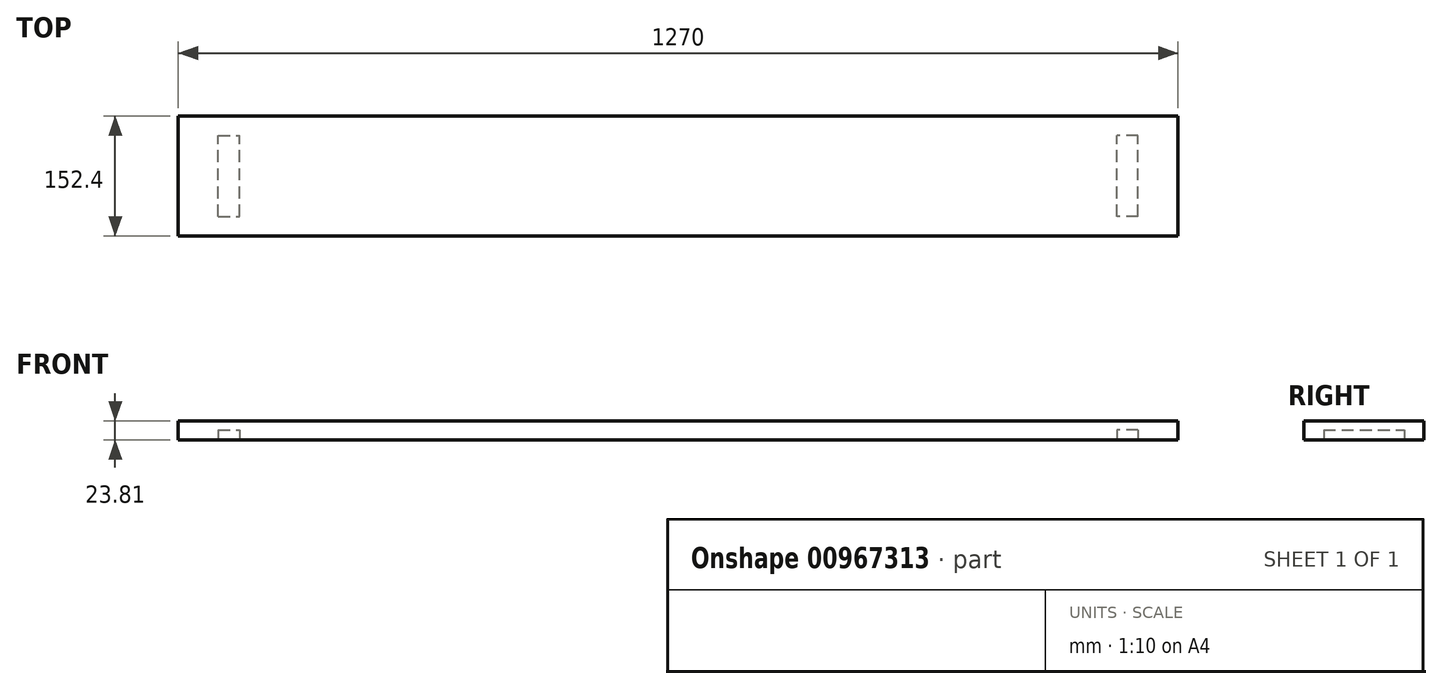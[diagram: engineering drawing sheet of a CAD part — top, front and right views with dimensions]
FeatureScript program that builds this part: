
annotation { "Feature Type Name" : "Feature", "Feature Type Description" : "" }
export const myFeature = defineFeature(function(context is Context, id is Id, definition is map)
    precondition{}
    {
        {
            var Q0;
            Q0=qCreatedBy(makeId("Top.planeOp"),FACE);
            var sketch = newSketch(context, id + "F0", { "sketchPlane" : qUnion([Q0])});
            skLineSegment(sketch, "E0.bottom", {"start": v(-909.25, -64.28) * mm, "end": v(360.75, -64.28) * mm});
            skLineSegment(sketch, "E0.top", {"start": v(-909.25, -216.68) * mm, "end": v(360.75, -216.68) * mm});
            skLineSegment(sketch, "E0.left", {"start": v(-909.25, -64.28) * mm, "end": v(-909.25, -216.68) * mm});
            skLineSegment(sketch, "E0.right", {"start": v(360.75, -64.28) * mm, "end": v(360.75, -216.68) * mm});
            skSolve(sketch);
        }
        {
            var Q0;
            Q0=makeQuery(id+"F0.imprint","IMPRINT",FACE,{"disambiguationData":[TD([[makeQuery(id+"F0.imprint","IMPRINT",EDGE,{"derivedFrom":sQuery(id+"F0.wireOp",EDGE,"E0.bottom")}),-1.0]])]});
            extrude(context, id + "F1", {"entities" : qUnion([Q0]), "depth" : 23.8 * mm, "offsetDistance" : 25.4 * mm});
        }
        {
            var Q0;
            Q0=makeQuery(id+"F1.opExtrude","CAP_FACE",FACE,{"disambiguationData":[OSD([sQuery(id+"F0.wireOp",EDGE,"E0.bottom"),sQuery(id+"F0.wireOp",EDGE,"E0.top"),sQuery(id+"F0.wireOp",EDGE,"E0.left"),sQuery(id+"F0.wireOp",EDGE,"E0.right")])],"isStart":true});
            var sketch = newSketch(context, id + "F2", { "sketchPlane" : qUnion([Q0])});
            skLineSegment(sketch, "E1.bottom", {"start": v(-858.45, 191.68) * mm, "end": v(-831.46, 191.68) * mm});
            skLineSegment(sketch, "E1.top", {"start": v(-858.45, 89.28) * mm, "end": v(-831.46, 89.28) * mm});
            skLineSegment(sketch, "E1.left", {"start": v(-858.45, 191.68) * mm, "end": v(-858.45, 89.28) * mm});
            skLineSegment(sketch, "E1.right", {"start": v(-831.46, 191.68) * mm, "end": v(-831.46, 89.28) * mm});
            skPoint(sketch, "E2", {"position": v(-909.25, 140.48) * mm});
            skPoint(sketch, "E3", {"position": v(-858.45, 140.48) * mm});
            skLineSegment(sketch, "E4", {"start": v(-274.25, 64.28) * mm, "end": v(-274.25, 216.68) * mm, "construction": true});
            skLineSegment(sketch, "E5.MirrorCS", {"start": v(282.97, 191.68) * mm, "end": v(282.97, 89.28) * mm});
            skLineSegment(sketch, "E6.MirrorCS", {"start": v(309.95, 89.28) * mm, "end": v(282.97, 89.28) * mm});
            skLineSegment(sketch, "E7.MirrorCS", {"start": v(309.95, 191.68) * mm, "end": v(309.95, 89.28) * mm});
            skLineSegment(sketch, "E8.MirrorCS", {"start": v(309.95, 191.68) * mm, "end": v(282.97, 191.68) * mm});
            skSolve(sketch);
        }
        {
            var Q0;
            Q0 = qSketchRegion(id + "F2", true);
            extrude(context, id + "F3", {"entities" : qUnion([Q0]), "operationType" : NewBodyOperationType.REMOVE, "oppositeDirection" : true, "depth" : 12.7 * mm, "offsetDistance" : 25.4 * mm});
        }
    });
